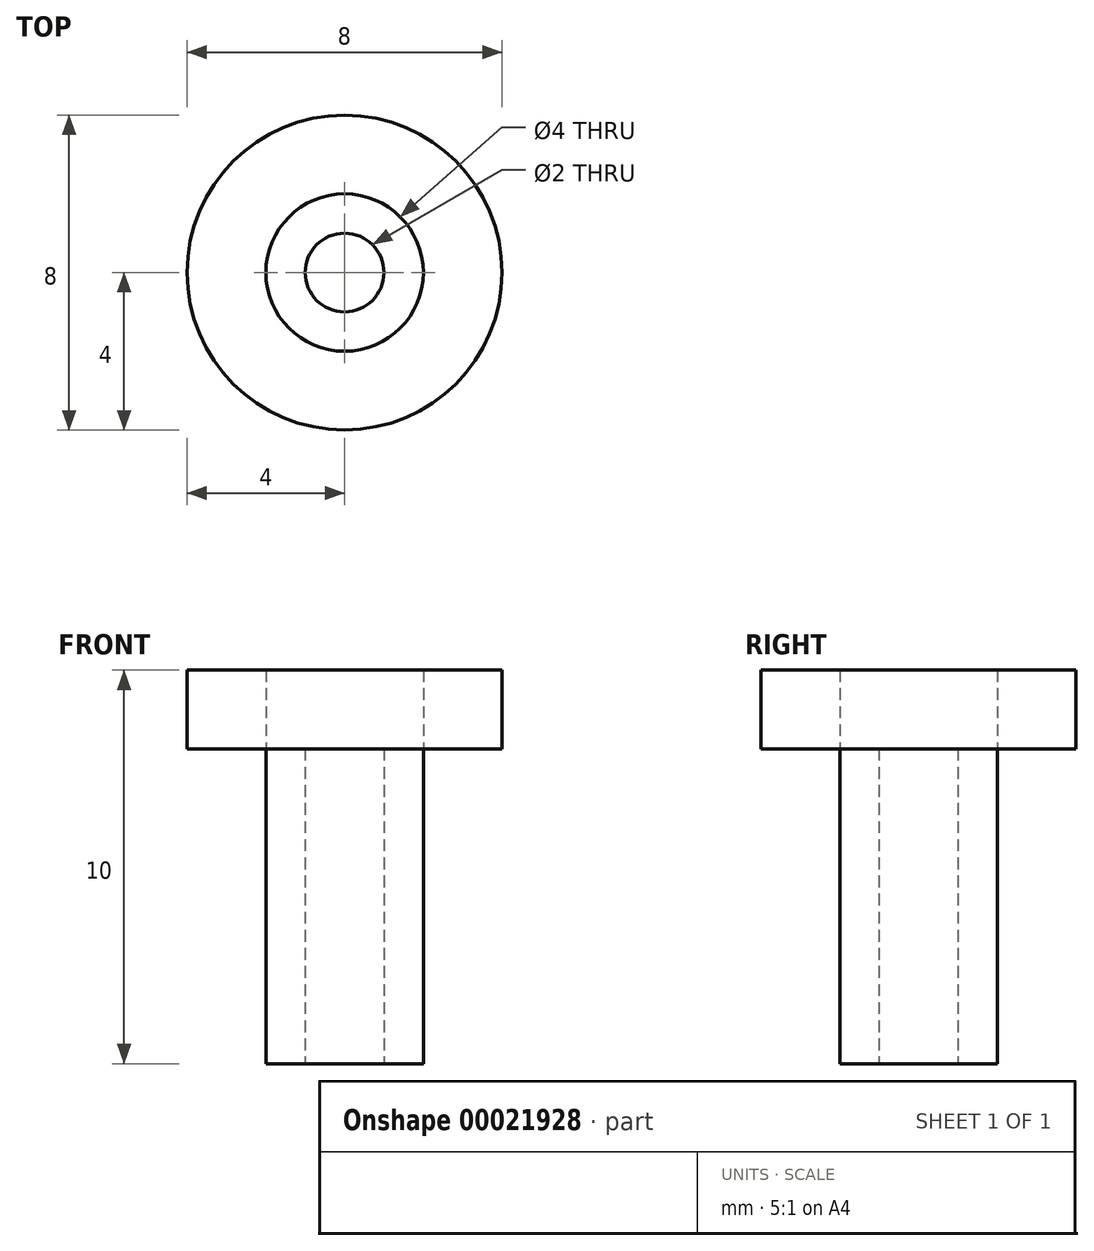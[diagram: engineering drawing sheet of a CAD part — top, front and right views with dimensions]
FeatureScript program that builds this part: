
annotation { "Feature Type Name" : "Feature", "Feature Type Description" : "" }
export const myFeature = defineFeature(function(context is Context, id is Id, definition is map)
    precondition{}
    {
        {
            var Q0;
            Q0=qCreatedBy(makeId("Top.planeOp"),FACE);
            var sketch = newSketch(context, id + "F0", { "sketchPlane" : qUnion([Q0])});
            skCircle(sketch, "E0", {"center": v(0, 0) * mm, "radius": 10 * mm});
            skCircle(sketch, "E1.1.1", {"center": v(0, 0) * mm, "radius": 20 * mm});
            skCircle(sketch, "E1.2.1", {"center": v(0, 0) * mm, "radius": 20 * mm});
            skCircle(sketch, "E1.3.1", {"center": v(0, 0) * mm, "radius": 20 * mm});
            skPoint(sketch, "E1.center", {"position": v(0, -0.72) * mm});
            skCircle(sketch, "E2", {"center": v(0, 0) * mm, "radius": 1 * mm});
            skCircle(sketch, "E3", {"center": v(0, 0) * mm, "radius": 2 * mm});
            skLineSegment(sketch, "E4", {"start": v(0, 0) * mm, "end": v(0, 3.5) * mm});
            skCircle(sketch, "E5", {"center": v(0, 5.5) * mm, "radius": 2 * mm});
            skCircle(sketch, "E6.1.0", {"center": v(-4.76, 2.75) * mm, "radius": 2 * mm});
            skCircle(sketch, "E6.2.0", {"center": v(-4.76, -2.75) * mm, "radius": 2 * mm});
            skCircle(sketch, "E6.3.0", {"center": v(0, -5.5) * mm, "radius": 2 * mm});
            skCircle(sketch, "E6.4.0", {"center": v(4.76, -2.75) * mm, "radius": 2 * mm});
            skCircle(sketch, "E6.5.0", {"center": v(4.76, 2.75) * mm, "radius": 2 * mm});
            skSolve(sketch);
        }
        {
            var Q0;
            Q0=makeQuery(id+"F0.imprint","IMPRINT",FACE,{"disambiguationData":[TD([[makeQuery(id+"F0.imprint","IMPRINT",EDGE,{"derivedFrom":sQuery(id+"F0.wireOp",EDGE,"E1.5.1")}),1.0]])]});
            var Q1;
            Q1=makeQuery(id+"F0.imprint","IMPRINT",FACE,{"disambiguationData":[TD([[makeQuery(id+"F0.imprint","IMPRINT",EDGE,{"derivedFrom":sQuery(id+"F0.wireOp",EDGE,"E2")}),-1.0]])]});
            extrude(context, id + "F1", {"entities" : qUnion([Q0, Q1]), "depth" : 6 * mm});
        }
        {
            var Q0;
            Q0=makeQuery(id+"F1.opExtrude","CAP_FACE",FACE,{"disambiguationData":[OSD([sQuery(id+"F0.wireOp",EDGE,"E1.5.1"),sQuery(id+"F0.wireOp",EDGE,"E2"),sQuery(id+"F0.wireOp",EDGE,"E5"),sQuery(id+"F0.wireOp",EDGE,"E6.1.0"),sQuery(id+"F0.wireOp",EDGE,"E6.2.0"),sQuery(id+"F0.wireOp",EDGE,"E6.3.0"),sQuery(id+"F0.wireOp",EDGE,"E6.4.0"),sQuery(id+"F0.wireOp",EDGE,"E6.5.0")])],"isStart":false});
            var sketch = newSketch(context, id + "F2", { "sketchPlane" : qUnion([Q0])});
            skCircle(sketch, "E7", {"center": v(0, 0) * mm, "radius": 4 * mm});
            skCircle(sketch, "E8", {"center": v(0, 0) * mm, "radius": 2 * mm});
            skSolve(sketch);
        }
        {
            var Q0;
            Q0=makeQuery(id+"F2.imprint","IMPRINT",FACE,{"disambiguationData":[TD([[makeQuery(id+"F2.imprint","IMPRINT",EDGE,{"derivedFrom":sQuery(id+"F2.wireOp",EDGE,"E7")}),1.0]])]});
            extrude(context, id + "F3", {"entities" : qUnion([Q0]), "operationType" : NewBodyOperationType.ADD, "depth" : 2 * mm});
        }
        {
            var Q0;
            Q0=makeQuery(id+"F0.imprint","IMPRINT",FACE,{"disambiguationData":[TD([[makeQuery(id+"F0.imprint","IMPRINT",EDGE,{"derivedFrom":sQuery(id+"F0.wireOp",EDGE,"E2")}),-1.0]])]});
            extrude(context, id + "F4", {"entities" : qUnion([Q0]), "operationType" : NewBodyOperationType.ADD, "depth" : 2 * mm});
        }
        {
            var Q0;
            Q0=makeQuery(id+"F0.imprint","IMPRINT",FACE,{"disambiguationData":[TD([[makeQuery(id+"F0.imprint","IMPRINT",EDGE,{"derivedFrom":sQuery(id+"F0.wireOp",EDGE,"E2")}),-1.0]])]});
            extrude(context, id + "F5", {"entities" : qUnion([Q0]), "operationType" : NewBodyOperationType.REMOVE, "oppositeDirection" : true, "depth" : 2 * mm});
        }
        {
            var Q0;
            Q0=makeQuery(id+"F0.imprint","IMPRINT",FACE,{"disambiguationData":[TD([[makeQuery(id+"F0.imprint","IMPRINT",EDGE,{"derivedFrom":sQuery(id+"F0.wireOp",EDGE,"E2")}),-1.0]])]});
            extrude(context, id + "F6", {"entities" : qUnion([Q0]), "operationType" : NewBodyOperationType.ADD, "oppositeDirection" : true, "depth" : 2 * mm});
        }
    });
